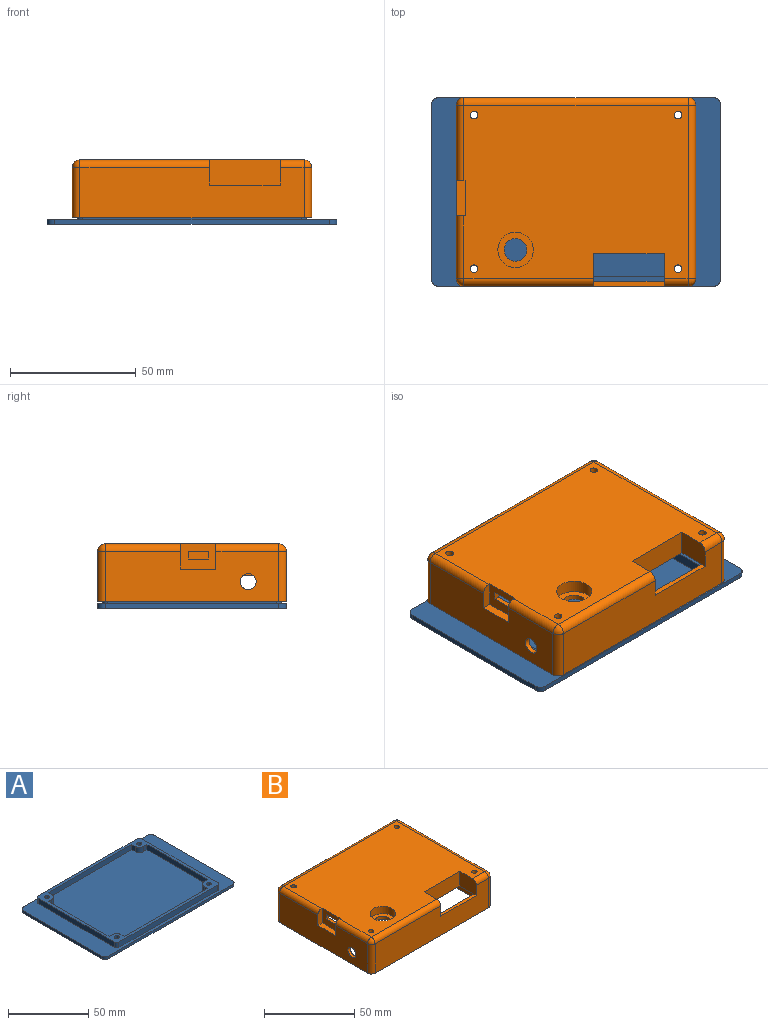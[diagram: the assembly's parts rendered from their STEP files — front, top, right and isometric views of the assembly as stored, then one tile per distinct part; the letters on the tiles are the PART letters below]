
ASSEMBLY  parts=2 mates=1
PART A: 48 faces, bbox 115x75x6 mm
  f0: plane 69x2mm, normal (-1,0,0), area 138mm2, adj f5,f22,f44,f47
  f1: plane 109x2mm, normal (0,-1,0), area 218mm2, adj f5,f22,f44,f45
  f2: plane 69x2mm, normal (1,0,0), area 138mm2, adj f5,f22,f45,f46
  f3: plane 109x2mm, normal (0,1,0), area 218mm2, adj f5,f22,f46,f47
  f4: plane 90.8x70.8mm, normal (0,0,1), area 765.9mm2, adj f6,f9,f12,f15,f18,f19,f20,f21
  f5: plane 115x75mm, normal (0,0,-1), area 8525.7mm2, adj f0,f1,f2,f3,f8,f11,f14,f17
  f6: cylinder r=1.5mm len=3mm, axis (0,0,-1), area 26.4mm2, adj f4,f7
  f7: plane 5.4x5.4mm, normal (0,0,-1), area 15.8mm2, adj f6,f8
  f8: cylinder r=2.7mm len=5.4mm, axis (0,0,-1), area 54.3mm2, adj f5,f7
  f9: cylinder r=1.5mm len=3mm, axis (0,0,-1), area 26.4mm2, adj f4,f10
  f10: plane 5.4x5.4mm, normal (0,0,-1), area 15.8mm2, adj f9,f11
  f11: cylinder r=2.7mm len=5.4mm, axis (0,0,-1), area 54.3mm2, adj f5,f10
  f12: cylinder r=1.5mm len=3mm, axis (0,0,-1), area 26.4mm2, adj f4,f13
  f13: plane 5.4x5.4mm, normal (0,0,-1), area 15.8mm2, adj f12,f14
  f14: cylinder r=2.7mm len=5.4mm, axis (0,0,-1), area 54.3mm2, adj f5,f13
  f15: cylinder r=1.5mm len=3mm, axis (0,0,-1), area 26.4mm2, adj f4,f16
  f16: plane 5.4x5.4mm, normal (0,0,-1), area 15.8mm2, adj f15,f17
  f17: cylinder r=2.7mm len=5.4mm, axis (0,0,-1), area 54.3mm2, adj f5,f16
  f18: plane 66.8x4mm, normal (-1,0,0), area 267.2mm2, adj f4,f22,f40,f43
  f19: plane 86.8x4mm, normal (0,1,0), area 347.2mm2, adj f4,f22,f40,f41
  f20: plane 66.8x4mm, normal (1,0,0), area 267.2mm2, adj f4,f22,f41,f42
  f21: plane 86.8x4mm, normal (0,-1,0), area 347.2mm2, adj f4,f22,f42,f43
  f22: plane 115x75mm, normal (0,0,1), area 2192.1mm2, adj f0,f1,f2,f3,f18,f19,f20,f21
  f23: plane 73.4x4mm, normal (0,1,0), area 293.6mm2, adj f4,f24,f38,f39
  f24: plane 4x2.9mm, normal (-1,0,0), area 11.6mm2, adj f4,f23,f25,f39
  f25: cylinder r=3.8mm len=4mm, axis (0,0,1), area 23.9mm2, adj f4,f24,f26,f39
  f26: plane 4x2.9mm, normal (0,1,0), area 11.6mm2, adj f4,f25,f27,f39
  f27: plane 53.4x4mm, normal (-1,0,0), area 213.6mm2, adj f4,f26,f28,f39
  f28: plane 4x2.9mm, normal (0,-1,0), area 11.6mm2, adj f4,f27,f29,f39
  f29: cylinder r=3.8mm len=4mm, axis (0,0,1), area 23.9mm2, adj f4,f28,f30,f39
  f30: plane 4x2.9mm, normal (-1,0,0), area 11.6mm2, adj f4,f29,f31,f39
  f31: plane 73.4x4mm, normal (0,-1,0), area 293.6mm2, adj f4,f30,f32,f39
  f32: plane 4x2.9mm, normal (1,0,0), area 11.6mm2, adj f4,f31,f33,f39
  f33: cylinder r=3.8mm len=4mm, axis (0,0,1), area 23.9mm2, adj f4,f32,f34,f39
  f34: plane 4x2.9mm, normal (0,-1,0), area 11.6mm2, adj f4,f33,f35,f39
  f35: plane 53.4x4mm, normal (1,0,0), area 213.6mm2, adj f4,f34,f36,f39
  f36: plane 4x2.9mm, normal (0,1,0), area 11.6mm2, adj f4,f35,f37,f39
  f37: cylinder r=3.8mm len=4mm, axis (0,0,1), area 23.9mm2, adj f4,f36,f38,f39
  f38: plane 4x2.9mm, normal (1,0,0), area 11.6mm2, adj f4,f23,f37,f39
  f39: plane 86.8x66.8mm, normal (0,0,1), area 5631.1mm2, adj f23,f24,f25,f26,f27,f28,f29,f30
  f40: cylinder r=2mm len=4mm, axis (0,0,-1), area 12.6mm2, adj f4,f18,f19,f22
  f41: cylinder r=2mm len=4mm, axis (0,0,1), area 12.6mm2, adj f4,f19,f20,f22
  f42: cylinder r=2mm len=4mm, axis (0,0,-1), area 12.6mm2, adj f4,f20,f21,f22
  f43: cylinder r=2mm len=4mm, axis (0,0,1), area 12.6mm2, adj f4,f18,f21,f22
  f44: cylinder r=3mm len=3mm, axis (0,0,1), area 9.4mm2, adj f0,f1,f5,f22
  f45: cylinder r=3mm len=3mm, axis (0,0,-1), area 9.4mm2, adj f1,f2,f5,f22
  f46: cylinder r=3mm len=3mm, axis (0,0,1), area 9.4mm2, adj f2,f3,f5,f22
  f47: cylinder r=3mm len=3mm, axis (0,0,-1), area 9.4mm2, adj f0,f3,f5,f22
PART B: 101 faces, bbox 95x75x23 mm
  f0: plane 69x20mm, normal (1,0,0), area 1158mm2, adj f2,f18,f19,f25,f85,f86,f87,f88
  f1: plane 69x20mm, normal (-1,0,0), area 1158mm2, adj f2,f46,f47,f53,f85,f86,f87,f88
  f2: plane 95x75mm, normal (0,0,-1), area 657.1mm2, adj f0,f1,f5,f6,f7,f17,f18,f19
  f3: plane 28x2mm, normal (0,0,1), area 56mm2, adj f6,f8,f9,f33
  f4: plane 89x69mm, normal (0,0,1), area 5671.8mm2, adj f8,f9,f10,f11,f14,f15,f16,f21
  f5: plane 69x20mm, normal (-1,0,0), area 1250.3mm2, adj f2,f13,f14,f15,f17,f20,f21,f30
  f6: plane 89x20mm, normal (0,-1,0), area 1584mm2, adj f2,f3,f8,f9,f17,f18,f27,f28
  f7: plane 89x20mm, normal (0,1,0), area 1475.2mm2, adj f2,f19,f20,f23,f69,f70,f71,f72
  f8: plane 13x10mm, normal (1,0,0), area 128.1mm2, adj f3,f4,f6,f10,f28,f35
  f9: plane 13x10mm, normal (-1,0,0), area 128.1mm2, adj f3,f4,f6,f10,f27,f35
  f10: plane 28x10mm, normal (0,-1,0), area 280mm2, adj f4,f8,f9,f35
  f11: cylinder r=7mm len=14mm, axis (0,0,1), area 219.9mm2, adj f4,f12
  f12: plane 14x14mm, normal (0,0,1), area 90.3mm2, adj f11,f59
  f13: plane 14x3.5mm, normal (0,0,1), area 49mm2, adj f5,f14,f15,f16
  f14: plane 10x3.5mm, normal (0,-1,0), area 33.1mm2, adj f4,f5,f13,f16,f21
  f15: plane 10x3.5mm, normal (0,1,0), area 33.1mm2, adj f4,f5,f13,f16,f30
  f16: plane 14x10mm, normal (-1,0,0), area 115.2mm2, adj f4,f13,f14,f15,f60,f61,f62,f63
  f17: cylinder r=3mm len=20mm, axis (0,0,1), area 94.2mm2, adj f2,f5,f6,f29
  f18: cylinder r=3mm len=20mm, axis (0,0,-1), area 94.2mm2, adj f0,f2,f6,f26
  f19: cylinder r=3mm len=20mm, axis (0,0,1), area 94.2mm2, adj f0,f2,f7,f24
  f20: cylinder r=3mm len=20mm, axis (0,0,-1), area 94.2mm2, adj f2,f5,f7,f22
  f21: cylinder r=3mm len=30mm, axis (0,1,0), area 141.4mm2, adj f4,f5,f14,f22
  f22: sphere r=3mm, area 14.1mm2, adj f20,f21,f23
  f23: cylinder r=3mm len=89mm, axis (1,0,0), area 419.4mm2, adj f4,f7,f22,f24
  f24: sphere r=3mm, area 14.1mm2, adj f19,f23,f25
  f25: cylinder r=3mm len=69mm, axis (0,-1,0), area 325.2mm2, adj f0,f4,f24,f26
  f26: sphere r=3mm, area 14.1mm2, adj f18,f25,f27
  f27: cylinder r=3mm len=9.5mm, axis (-1,0,0), area 44.8mm2, adj f4,f6,f9,f26
  f28: cylinder r=3mm len=51.5mm, axis (-1,0,0), area 242.7mm2, adj f4,f6,f8,f29
  f29: sphere r=3mm, area 14.1mm2, adj f17,f28,f30
  f30: cylinder r=3mm len=25mm, axis (0,1,0), area 117.8mm2, adj f4,f5,f15,f29
  f31: plane 89x69mm, normal (0,0,-1), area 5429.3mm2, adj f36,f37,f38,f39,f42,f43,f44,f49
  f32: plane 69x20mm, normal (1,0,0), area 1186.3mm2, adj f2,f41,f42,f43,f45,f48,f49,f58
  f33: plane 89x20mm, normal (0,1,0), area 1556mm2, adj f2,f3,f35,f36,f37,f45,f46,f55
  f34: plane 89x20mm, normal (0,-1,0), area 1475.2mm2, adj f2,f47,f48,f51,f69,f70,f71,f72
  f35: plane 32x13mm, normal (0,0,-1), area 108mm2, adj f8,f9,f10,f33,f36,f37,f38
  f36: plane 13x8mm, normal (-1,0,0), area 103.8mm2, adj f31,f33,f35,f38,f56
  f37: plane 13x8mm, normal (1,0,0), area 103.8mm2, adj f31,f33,f35,f38,f55
  f38: plane 32x8mm, normal (0,1,0), area 256mm2, adj f31,f35,f36,f37
  f39: cylinder r=9mm len=18mm, axis (0,0,1), area 282.7mm2, adj f31,f40
  f40: plane 18x18mm, normal (0,0,-1), area 190.9mm2, adj f39,f59
  f41: plane 18x3.5mm, normal (0,0,-1), area 63mm2, adj f32,f42,f43,f44
  f42: plane 10x3.5mm, normal (0,1,0), area 34.8mm2, adj f31,f32,f41,f44,f49
  f43: plane 10x3.5mm, normal (0,-1,0), area 34.8mm2, adj f31,f32,f41,f44,f58
  f44: plane 18x10mm, normal (1,0,0), area 155.2mm2, adj f31,f41,f42,f43,f60,f61,f62,f63
  f45: cylinder r=1mm len=20mm, axis (0,0,1), area 31.4mm2, adj f2,f32,f33,f57
  f46: cylinder r=1mm len=20mm, axis (0,0,-1), area 31.4mm2, adj f1,f2,f33,f54
  f47: cylinder r=1mm len=20mm, axis (0,0,1), area 31.4mm2, adj f1,f2,f34,f52
  f48: cylinder r=1mm len=20mm, axis (0,0,-1), area 31.4mm2, adj f2,f32,f34,f50
  f49: cylinder r=1mm len=28mm, axis (0,1,0), area 44mm2, adj f31,f32,f42,f50
  f50: sphere r=1mm, area 1.6mm2, adj f48,f49,f51
  f51: cylinder r=1mm len=89mm, axis (1,0,0), area 139.8mm2, adj f31,f34,f50,f52
  f52: sphere r=1mm, area 1.6mm2, adj f47,f51,f53
  f53: cylinder r=1mm len=69mm, axis (0,-1,0), area 108.4mm2, adj f1,f31,f52,f54
  f54: sphere r=1mm, area 1.6mm2, adj f46,f53,f55
  f55: cylinder r=1mm len=7.5mm, axis (-1,0,0), area 11.8mm2, adj f31,f33,f37,f54
  f56: cylinder r=1mm len=49.5mm, axis (-1,0,0), area 77.8mm2, adj f31,f33,f36,f57
  f57: sphere r=1mm, area 1.6mm2, adj f45,f56,f58
  f58: cylinder r=1mm len=23mm, axis (0,1,0), area 36.1mm2, adj f31,f32,f43,f57
  f59: cylinder r=4.5mm len=9mm, axis (0,0,1), area 56.5mm2, adj f12,f40
  f60: plane 3.1x2mm, normal (0,-1,0), area 6.2mm2, adj f16,f44,f61,f62
  f61: plane 8x2mm, normal (0,0,-1), area 16mm2, adj f16,f44,f60,f63
  f62: plane 8x2mm, normal (0,0,1), area 16mm2, adj f16,f44,f60,f63
  f63: plane 3.1x2mm, normal (0,1,0), area 6.2mm2, adj f16,f44,f61,f62
  f64: cylinder r=1.5mm len=3mm, axis (0,0,1), area 18.8mm2, adj f4,f31
  f65: cylinder r=1.5mm len=3mm, axis (0,0,1), area 18.8mm2, adj f4,f31
  f66: cylinder r=1.5mm len=3mm, axis (0,0,1), area 18.8mm2, adj f4,f31
  f67: cylinder r=1.5mm len=3mm, axis (0,0,1), area 18.8mm2, adj f4,f31
  f68: cylinder r=3.17mm len=6.35mm, axis (-1,0,0), area 39.9mm2, adj f5,f32
  f69: plane 6x2mm, normal (1,0,0), area 12mm2, adj f7,f34,f70,f71
  f70: plane 12.7x2mm, normal (0,0,1), area 25.4mm2, adj f7,f34,f69,f72
  f71: plane 12.7x2mm, normal (0,0,-1), area 25.4mm2, adj f7,f34,f69,f72
  f72: plane 6x2mm, normal (-1,0,0), area 12mm2, adj f7,f34,f70,f71
  f73: plane 6x2mm, normal (1,0,0), area 12mm2, adj f7,f34,f74,f75
  f74: plane 12.7x2mm, normal (0,0,1), area 25.4mm2, adj f7,f34,f73,f76
  f75: plane 12.7x2mm, normal (0,0,-1), area 25.4mm2, adj f7,f34,f73,f76
  f76: plane 6x2mm, normal (-1,0,0), area 12mm2, adj f7,f34,f74,f75
  f77: plane 6x2mm, normal (1,0,0), area 12mm2, adj f7,f34,f78,f79
  f78: plane 12.7x2mm, normal (0,0,1), area 25.4mm2, adj f7,f34,f77,f80
  f79: plane 12.7x2mm, normal (0,0,-1), area 25.4mm2, adj f7,f34,f77,f80
  f80: plane 6x2mm, normal (-1,0,0), area 12mm2, adj f7,f34,f78,f79
  f81: plane 6x2mm, normal (1,0,0), area 12mm2, adj f7,f34,f82,f83
  f82: plane 12.7x2mm, normal (0,0,1), area 25.4mm2, adj f7,f34,f81,f84
  f83: plane 12.7x2mm, normal (0,0,-1), area 25.4mm2, adj f7,f34,f81,f84
  f84: plane 6x2mm, normal (-1,0,0), area 12mm2, adj f7,f34,f82,f83
  f85: plane 6x2mm, normal (0,1,0), area 12mm2, adj f0,f1,f86,f88
  f86: plane 10.5x2mm, normal (0,0,1), area 21mm2, adj f0,f1,f85,f87
  f87: plane 6x2mm, normal (0,-1,0), area 12mm2, adj f0,f1,f86,f88
  f88: plane 10.5x2mm, normal (0,0,-1), area 21mm2, adj f0,f1,f85,f87
  f89: plane 6x2mm, normal (0,1,0), area 12mm2, adj f0,f1,f90,f92
  f90: plane 10.5x2mm, normal (0,0,1), area 21mm2, adj f0,f1,f89,f91
  f91: plane 6x2mm, normal (0,-1,0), area 12mm2, adj f0,f1,f90,f92
  f92: plane 10.5x2mm, normal (0,0,-1), area 21mm2, adj f0,f1,f89,f91
  f93: plane 6x2mm, normal (0,1,0), area 12mm2, adj f0,f1,f94,f96
  f94: plane 8x2mm, normal (0,0,1), area 16mm2, adj f0,f1,f93,f95
  f95: plane 6x2mm, normal (0,-1,0), area 12mm2, adj f0,f1,f94,f96
  f96: plane 8x2mm, normal (0,0,-1), area 16mm2, adj f0,f1,f93,f95
  f97: plane 6x2mm, normal (0,1,0), area 12mm2, adj f0,f1,f98,f100
  f98: plane 8x2mm, normal (0,0,1), area 16mm2, adj f0,f1,f97,f99
  f99: plane 6x2mm, normal (0,-1,0), area 12mm2, adj f0,f1,f98,f100
  f100: plane 8x2mm, normal (0,0,-1), area 16mm2, adj f0,f1,f97,f99
PLACE A t=(-57.5,-37.5,0)mm
PLACE B t=(-47.5,-37.5,2.5)mm
MATE fastened A.f9 <-> B.f67  axis (0,0,1) through (40.5,-30.5,6)mm
